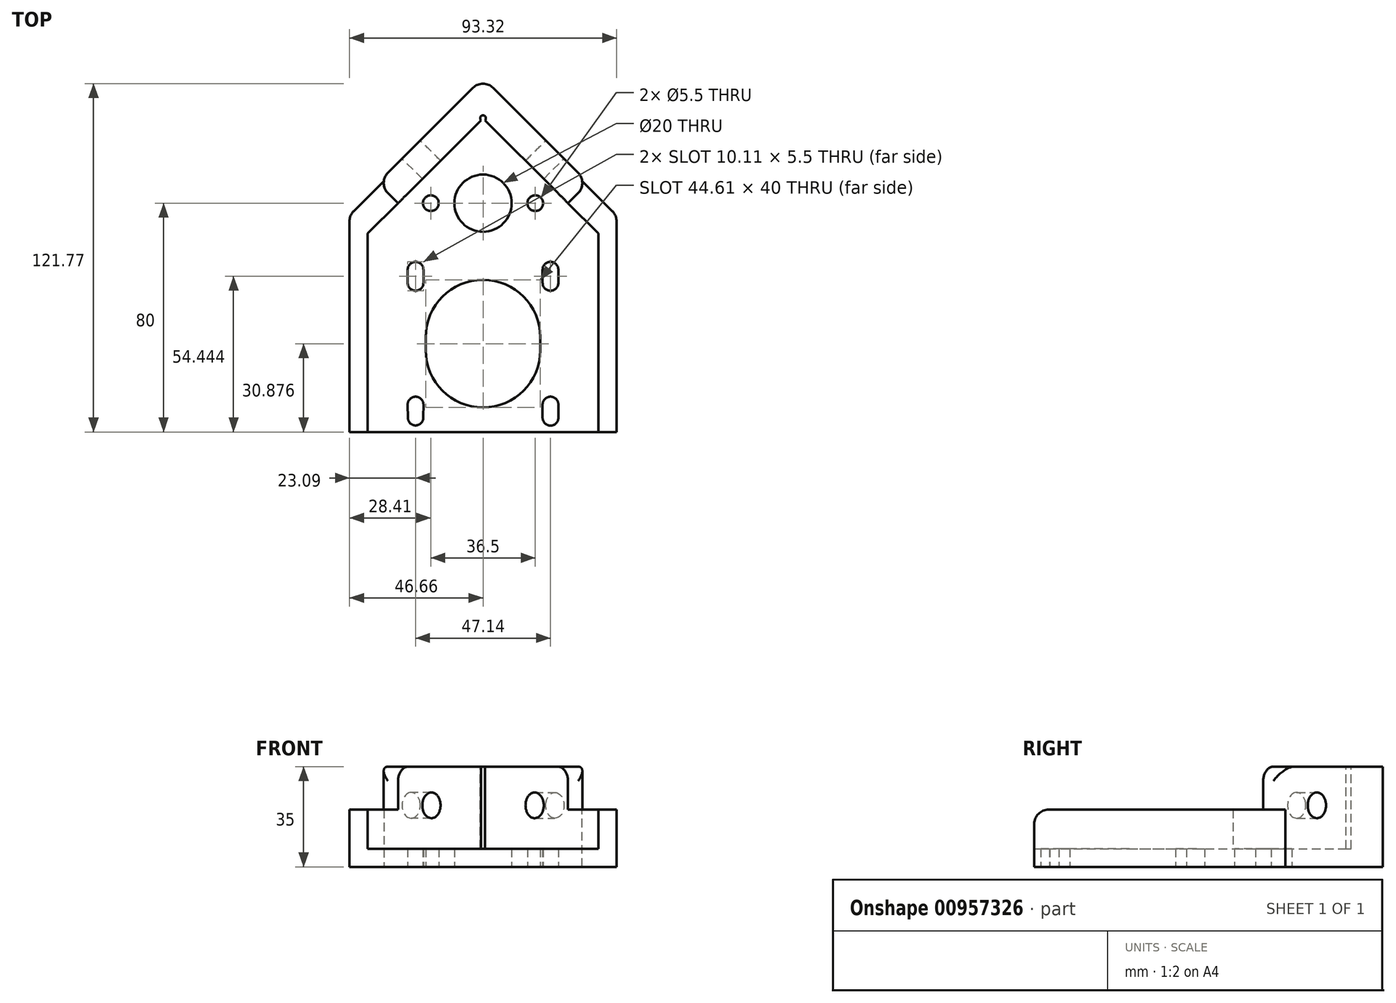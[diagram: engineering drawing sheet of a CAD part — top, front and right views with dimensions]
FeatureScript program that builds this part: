
annotation { "Feature Type Name" : "Feature", "Feature Type Description" : "" }
export const myFeature = defineFeature(function(context is Context, id is Id, definition is map)
    precondition{}
    {
        {
            var Q0;
            Q0=qCreatedBy(makeId("Top.planeOp"),FACE);
            var sketch = newSketch(context, id + "F0", { "sketchPlane" : qUnion([Q0])});
            skLineSegment(sketch, "E0", {"start": v(-29.7, 70) * mm, "end": v(0, 99.7) * mm});
            skLineSegment(sketch, "E1", {"start": v(0, 99.7) * mm, "end": v(0, 0) * mm, "construction": true});
            skCircle(sketch, "E2", {"center": v(0, 70) * mm, "radius": 10 * mm});
            skLineSegment(sketch, "E3", {"start": v(0, 70) * mm, "end": v(0, 99.7) * mm, "construction": true});
            skLineSegment(sketch, "E4", {"start": v(0, 99.7) * mm, "end": v(-29.7, 70) * mm, "construction": true});
            skLineSegment(sketch, "E5", {"start": v(-29.7, 70) * mm, "end": v(0, 40.3) * mm, "construction": true});
            skLineSegment(sketch, "E6", {"start": v(0, 88.25) * mm, "end": v(-18.25, 70) * mm, "construction": true});
            skLineSegment(sketch, "E7", {"start": v(-18.25, 70) * mm, "end": v(0, 51.75) * mm, "construction": true});
            skArc(sketch, "E8", {"start": v(-20.82, 46.75) * mm, "mid": v(-23.57, 49.5) * mm, "end": v(-26.32, 46.75) * mm});
            skCircle(sketch, "E9", {"center": v(-18.25, 70) * mm, "radius": 2.75 * mm});
            skLineSegment(sketch, "E10.MirrorCS", {"start": v(29.7, 70) * mm, "end": v(0, 99.7) * mm});
            skCircle(sketch, "E11.MirrorC", {"center": v(18.25, 70) * mm, "radius": 2.75 * mm});
            skArc(sketch, "E12.MirrorC", {"start": v(20.82, 46.75) * mm, "mid": v(23.57, 49.5) * mm, "end": v(26.32, 46.75) * mm});
            skLineSegment(sketch, "E13.MirrorCS", {"start": v(0, 99.7) * mm, "end": v(29.7, 70) * mm, "construction": true});
            skLineSegment(sketch, "E14.MirrorCS", {"start": v(0, 88.25) * mm, "end": v(18.25, 70) * mm, "construction": true});
            skLineSegment(sketch, "E15.MirrorCS", {"start": v(18.25, 70) * mm, "end": v(0, 51.75) * mm, "construction": true});
            skLineSegment(sketch, "E16.MirrorCS", {"start": v(29.7, 70) * mm, "end": v(0, 40.3) * mm, "construction": true});
            skLineSegment(sketch, "E17", {"start": v(-29.64, 23.18) * mm, "end": v(29.64, 23.18) * mm, "construction": true});
            skArc(sketch, "E18.MirrorC", {"start": v(26.32, -0.4) * mm, "mid": v(23.58, 2.36) * mm, "end": v(20.82, -0.39) * mm});
            skArc(sketch, "E19.MirrorC", {"start": v(-26.32, -0.42) * mm, "mid": v(-23.56, 2.36) * mm, "end": v(-20.82, -0.44) * mm});
            skLineSegment(sketch, "E20", {"start": v(-29.7, 70) * mm, "end": v(-29.7, -10) * mm});
            skLineSegment(sketch, "E21", {"start": v(-29.7, -10) * mm, "end": v(29.7, -10) * mm});
            skLineSegment(sketch, "E22", {"start": v(29.7, -10) * mm, "end": v(29.7, 70) * mm});
            skArc(sketch, "E23", {"start": v(-26.32, 42.14) * mm, "mid": v(-23.57, 39.39) * mm, "end": v(-20.82, 42.14) * mm});
            skArc(sketch, "E24.MirrorC", {"start": v(26.32, 42.14) * mm, "mid": v(23.57, 39.39) * mm, "end": v(20.82, 42.14) * mm});
            skArc(sketch, "E25.MirrorC", {"start": v(20.82, -5) * mm, "mid": v(23.78, -7.74) * mm, "end": v(26.3, -4.59) * mm});
            skArc(sketch, "E26.MirrorC", {"start": v(-20.9, -4.73) * mm, "mid": v(-23.42, -7.69) * mm, "end": v(-26.26, -5.03) * mm});
            skLineSegment(sketch, "E27", {"start": v(-26.32, 46.75) * mm, "end": v(-26.32, 42.14) * mm});
            skLineSegment(sketch, "E28", {"start": v(-20.82, 46.75) * mm, "end": v(-20.82, 42.14) * mm});
            skLineSegment(sketch, "E29", {"start": v(20.82, 46.75) * mm, "end": v(20.82, 42.14) * mm});
            skLineSegment(sketch, "E30", {"start": v(26.32, 46.75) * mm, "end": v(26.32, 42.14) * mm});
            skLineSegment(sketch, "E31", {"start": v(-26.32, -0.42) * mm, "end": v(-26.26, -5.03) * mm});
            skLineSegment(sketch, "E32", {"start": v(-20.82, -0.44) * mm, "end": v(-20.9, -4.73) * mm});
            skLineSegment(sketch, "E33", {"start": v(20.82, -0.39) * mm, "end": v(20.82, -5) * mm});
            skLineSegment(sketch, "E34", {"start": v(26.32, -0.4) * mm, "end": v(26.3, -4.59) * mm});
            skArc(sketch, "E35", {"start": v(20, 23.18) * mm, "mid": v(0, 43.18) * mm, "end": v(-20, 23.18) * mm});
            skArc(sketch, "E36", {"start": v(-20, 18.57) * mm, "mid": v(0, -1.43) * mm, "end": v(20, 18.57) * mm});
            skLineSegment(sketch, "E37", {"start": v(-20, 23.18) * mm, "end": v(-20, 18.57) * mm});
            skLineSegment(sketch, "E38", {"start": v(20, 23.18) * mm, "end": v(20, 18.57) * mm});
            skSolve(sketch);
        }
        {
            var Q0;
            Q0=makeQuery(id+"F0.imprint","IMPRINT",FACE,{"disambiguationData":[TD([[makeQuery(id+"F0.imprint","IMPRINT",EDGE,{"derivedFrom":sQuery(id+"F0.wireOp",EDGE,"E0")}),-1.0]])]});
            extrude(context, id + "F1", {"entities" : qUnion([Q0]), "depth" : 6.35 * mm, "offsetDistance" : 25 * mm});
        }
        {
            var Q0;
            Q0=qCreatedBy(makeId("Top.planeOp"),FACE);
            var sketch = newSketch(context, id + "F2", { "sketchPlane" : qUnion([Q0])});
            skLineSegment(sketch, "E39", {"start": v(0, 99.7) * mm, "end": v(-46.66, 53.04) * mm});
            skLineSegment(sketch, "E40", {"start": v(-46.66, 53.04) * mm, "end": v(-46.66, -10) * mm});
            skLineSegment(sketch, "E41", {"start": v(-46.66, -10) * mm, "end": v(0, -10) * mm});
            skLineSegment(sketch, "E42", {"start": v(-40.3, 59.4) * mm, "end": v(-40.3, -10) * mm});
            skLineSegment(sketch, "E43", {"start": v(0, 99.7) * mm, "end": v(0, 112.43) * mm});
            skLineSegment(sketch, "E44", {"start": v(0, 112.43) * mm, "end": v(-46.66, 65.77) * mm});
            skLineSegment(sketch, "E45", {"start": v(-46.66, 65.77) * mm, "end": v(-46.66, 53.04) * mm});
            skLineSegment(sketch, "E46.MirrorCS", {"start": v(0, 99.7) * mm, "end": v(46.66, 53.04) * mm});
            skLineSegment(sketch, "E47.MirrorCS", {"start": v(40.3, 59.4) * mm, "end": v(40.3, -10) * mm});
            skLineSegment(sketch, "E48.MirrorCS", {"start": v(0, 112.43) * mm, "end": v(46.66, 65.77) * mm});
            skLineSegment(sketch, "E49.MirrorCS", {"start": v(46.66, 53.04) * mm, "end": v(46.66, -10) * mm});
            skLineSegment(sketch, "E50.MirrorCS", {"start": v(46.66, -10) * mm, "end": v(0, -10) * mm});
            skLineSegment(sketch, "E51.MirrorCS", {"start": v(46.66, 65.77) * mm, "end": v(46.66, 53.04) * mm});
            skLineSegment(sketch, "E52", {"start": v(-29.7, 70) * mm, "end": v(-29.7, -10) * mm});
            skLineSegment(sketch, "E53", {"start": v(29.7, 70) * mm, "end": v(29.7, -10) * mm});
            skSolve(sketch);
        }
        {
            var Q0;
            Q0=makeQuery(id+"F2.imprint","IMPRINT",FACE,{"disambiguationData":[TD([[makeQuery(id+"F2.imprint","IMPRINT",EDGE,{"derivedFrom":sQuery(id+"F2.wireOp",EDGE,"E44")}),1.0]])]});
            var Q1;
            {var subQ0=sQuery(id+"F2.wireOp",EDGE,"E42");Q1=makeQuery(id+"F2.imprint","IMPRINT",FACE,{"disambiguationData":[TD([[makeQuery(id+"F2.imprint","IMPRINT",EDGE,{"derivedFrom":subQ0}),1.0]])]});}
            var Q2;
            {var subQ0=sQuery(id+"F2.wireOp",EDGE,"E40");Q2=makeQuery(id+"F2.imprint","IMPRINT",FACE,{"disambiguationData":[TD([[makeQuery(id+"F2.imprint","IMPRINT",EDGE,{"derivedFrom":subQ0}),1.0]])]});}
            var Q3;
            {var subQ0=sQuery(id+"F2.wireOp",EDGE,"E47.MirrorCS");Q3=makeQuery(id+"F2.imprint","IMPRINT",FACE,{"disambiguationData":[TD([[makeQuery(id+"F2.imprint","IMPRINT",EDGE,{"derivedFrom":subQ0}),-1.0]])]});}
            var Q4;
            {var subQ2=sQuery(id+"F2.wireOp",EDGE,"E47.MirrorCS");Q4=makeQuery(id+"F2.imprint","IMPRINT",FACE,{"disambiguationData":[TD([[makeQuery(id+"F2.imprint","IMPRINT",EDGE,{"derivedFrom":subQ2}),1.0]])]});}
            var Q5;
            Q5=makeQuery(id+"F2.imprint","IMPRINT",FACE,{"disambiguationData":[TD([[makeQuery(id+"F2.imprint","IMPRINT",EDGE,{"derivedFrom":sQuery(id+"F2.wireOp",EDGE,"E48.MirrorCS")}),-1.0]])]});
            extrude(context, id + "F3", {"entities" : qUnion([Q0, Q1, Q2, Q3, Q4, Q5]), "operationType" : NewBodyOperationType.ADD, "depth" : 6.35 * mm, "offsetDistance" : 25 * mm});
        }
        {
            var Q0;
            {var subQ2=sQuery(id+"F2.wireOp",EDGE,"E47.MirrorCS");Q0=makeQuery(id+"F2.imprint","IMPRINT",FACE,{"disambiguationData":[TD([[makeQuery(id+"F2.imprint","IMPRINT",EDGE,{"derivedFrom":subQ2}),1.0]])]});}
            var Q1;
            {var subQ0=sQuery(id+"F2.wireOp",EDGE,"E40");Q1=makeQuery(id+"F2.imprint","IMPRINT",FACE,{"disambiguationData":[TD([[makeQuery(id+"F2.imprint","IMPRINT",EDGE,{"derivedFrom":subQ0}),1.0]])]});}
            var Q2;
            Q2=makeQuery(id+"F2.imprint","IMPRINT",FACE,{"disambiguationData":[TD([[makeQuery(id+"F2.imprint","IMPRINT",EDGE,{"derivedFrom":sQuery(id+"F2.wireOp",EDGE,"E48.MirrorCS")}),-1.0]])]});
            var Q3;
            Q3=makeQuery(id+"F2.imprint","IMPRINT",FACE,{"disambiguationData":[TD([[makeQuery(id+"F2.imprint","IMPRINT",EDGE,{"derivedFrom":sQuery(id+"F2.wireOp",EDGE,"E44")}),1.0]])]});
            extrude(context, id + "F4", {"entities" : qUnion([Q0, Q1, Q2, Q3]), "operationType" : NewBodyOperationType.ADD, "depth" : 20 * mm, "offsetDistance" : 25 * mm});
        }
        {
            var Q0;
            Q0=makeQuery(id+"F1.opExtrude","CAP_FACE",FACE,{"disambiguationData":[OSD([sQuery(id+"F0.wireOp",EDGE,"CqNvWhCR-X9q0-hkb6-Y5B6-FddO2p67PmDH"),sQuery(id+"F0.wireOp",EDGE,"OIBRXke7-KifX-nYgX-6AyS-i8wfslzJrOtY"),sQuery(id+"F0.wireOp",EDGE,"E0"),sQuery(id+"F0.wireOp",EDGE,"E2"),sQuery(id+"F0.wireOp",EDGE,"E8"),sQuery(id+"F0.wireOp",EDGE,"E9"),sQuery(id+"F0.wireOp",EDGE,"E10.MirrorCS"),sQuery(id+"F0.wireOp",EDGE,"2e774edb-d105-46dc-81d8-f344b8156d9b1.MirrorCS"),sQuery(id+"F0.wireOp",EDGE,"2e774edb-d105-46dc-81d8-f344b8156d9b2.MirrorCS"),sQuery(id+"F0.wireOp",EDGE,"2e774edb-d105-46dc-81d8-f344b8156d9b3.MirrorC"),sQuery(id+"F0.wireOp",EDGE,"2e774edb-d105-46dc-81d8-f344b8156d9b6.MirrorC"),sQuery(id+"F0.wireOp",EDGE,"E11.MirrorC"),sQuery(id+"F0.wireOp",EDGE,"E12.MirrorC")])],"isStart":true});
            var sketch = newSketch(context, id + "F5", { "sketchPlane" : qUnion([Q0])});
            skLineSegment(sketch, "E54", {"start": v(-29.7, -70) * mm, "end": v(-36.77, -77.07) * mm});
            skLineSegment(sketch, "E55", {"start": v(-36.77, -77.07) * mm, "end": v(-5.84, -108) * mm});
            skLineSegment(sketch, "E56", {"start": v(0, -70) * mm, "end": v(-10, -70) * mm, "construction": true});
            skLineSegment(sketch, "E57", {"start": v(0, -108) * mm, "end": v(0, -70) * mm, "construction": true});
            skLineSegment(sketch, "E58.MirrorCS", {"start": v(0, -70) * mm, "end": v(10, -70) * mm, "construction": true});
            skLineSegment(sketch, "E59.MirrorCS", {"start": v(36.77, -77.07) * mm, "end": v(5.84, -108) * mm});
            skLineSegment(sketch, "E60.MirrorCS", {"start": v(29.7, -70) * mm, "end": v(36.77, -77.07) * mm});
            skLineSegment(sketch, "E61", {"start": v(-29.7, -70) * mm, "end": v(0, -99.7) * mm});
            skLineSegment(sketch, "E62", {"start": v(0, -99.7) * mm, "end": v(29.7, -70) * mm});
            skLineSegment(sketch, "E63", {"start": v(-5.84, -108) * mm, "end": v(0, -113.84) * mm});
            skLineSegment(sketch, "E64", {"start": v(0, -113.84) * mm, "end": v(5.84, -108) * mm});
            skSolve(sketch);
        }
        {
            var Q0;
            Q0=qSketchRegion(id+"F5",true);
            extrude(context, id + "F6", {"entities" : qUnion([Q0]), "operationType" : NewBodyOperationType.ADD, "oppositeDirection" : true, "depth" : 35 * mm, "offsetDistance" : 25 * mm});
        }
        {
            var Q0;
            Q0=makeQuery(id+"F6.opExtrude","SWEPT_FACE",FACE,{"disambiguationData":[OSD([sQuery(id+"F5.wireOp",EDGE,"E59.MirrorCS")])]});
            var sketch = newSketch(context, id + "F7", { "sketchPlane" : qUnion([Q0])});
            skCircle(sketch, "E65", {"center": v(45, 21.5) * mm, "radius": 4.5 * mm});
            skSolve(sketch);
        }
        {
            var Q0;
            Q0=qSketchRegion(id+"F7",true);
            extrude(context, id + "F8", {"entities" : qUnion([Q0]), "oppositeDirection" : true, "depth" : 12.6 * mm, "offsetDistance" : 25 * mm});
        }
        {
            var Q0;
            Q0=makeQuery(id+"F6.opExtrude","CAP_EDGE",EDGE,{"disambiguationData":[OSD([sQuery(id+"F5.wireOp",EDGE,"E60.MirrorCS")])],"isStart":false});
            var Q1;
            Q1=makeQuery(id+"F6.opExtrude","CAP_EDGE",EDGE,{"disambiguationData":[OSD([sQuery(id+"F5.wireOp",EDGE,"E54")])],"isStart":false});
            var Q2;
            Q2=makeQuery(id+"F6.opExtrude","SWEPT_EDGE",EDGE,{"disambiguationData":[OSD([sQuery(id+"F5.wireOp",EDGE,"E55"),sQuery(id+"F5.wireOp",EDGE,"w3E64LNr-WMrx-ZLcy-Yoss-pTT7xmLwoX0f")])]});
            var Q3;
            Q3=makeQuery(id+"F6.opExtrude","SWEPT_EDGE",EDGE,{"disambiguationData":[OSD([sQuery(id+"F5.wireOp",EDGE,"90518d0a-a1d5-48df-ab97-8c912662351c1.MirrorCS"),sQuery(id+"F5.wireOp",EDGE,"E59.MirrorCS")])]});
            var Q4;
            Q4=makeQuery(id+"F4.opExtrude","SWEPT_EDGE",EDGE,{"disambiguationData":[OSD([sQuery(id+"F2.wireOp",EDGE,"2lfpNZEj-ZkGW-H239-BTSb-PnOlReioI05R"),sQuery(id+"F2.wireOp",EDGE,"Y7oqJvWZ-fw66-fsUm-KreW-a8dZiDZSDvyh")])]});
            var Q5;
            Q5=makeQuery(id+"F4.opExtrude","SWEPT_EDGE",EDGE,{"disambiguationData":[OSD([sQuery(id+"F2.wireOp",EDGE,"28NQsGmG-He18-9Lgd-yZ6g-9qgcsKt1NNAv"),sQuery(id+"F2.wireOp",EDGE,"8z5xyMcj-PstS-gyoc-Zbjk-fvMzcH1uuJEM"),sQuery(id+"F2.wireOp",EDGE,"Y7oqJvWZ-fw66-fsUm-KreW-a8dZiDZSDvyh")])]});
            var Q6;
            Q6=makeQuery(id+"F4.opExtrude","SWEPT_EDGE",EDGE,{"disambiguationData":[OSD([sQuery(id+"F2.wireOp",EDGE,"f8a4cf56-4e17-4c88-a3d7-404ae4d5c7f90.MirrorCS"),sQuery(id+"F2.wireOp",EDGE,"8ee5f7fc-c1b9-4571-8d56-7bdf9bbc2ac70.MirrorCS")])]});
            var Q7;
            Q7=makeQuery(id+"F4.opExtrude","SWEPT_EDGE",EDGE,{"disambiguationData":[OSD([sQuery(id+"F2.wireOp",EDGE,"1d0ece78-aebc-48e7-a5a8-8e38171d103b0.MirrorCS"),sQuery(id+"F2.wireOp",EDGE,"a64d8b8a-c93f-4d5a-9a8b-79496ac34db30.MirrorCS"),sQuery(id+"F2.wireOp",EDGE,"8ee5f7fc-c1b9-4571-8d56-7bdf9bbc2ac70.MirrorCS")])]});
            var Q8;
            Q8=makeQuery(id+"F4.opExtrude","CAP_EDGE",EDGE,{"disambiguationData":[OSD([sQuery(id+"F2.wireOp",EDGE,"E50.MirrorCS")])],"isStart":false});
            var Q9;
            Q9=makeQuery(id+"F4.opExtrude","CAP_EDGE",EDGE,{"disambiguationData":[OSD([sQuery(id+"F2.wireOp",EDGE,"E41")])],"isStart":false});
            var Q10;
            {var subQ0=sQuery(id+"F2.wireOp",EDGE,"E51.MirrorCS");var subQ1=sQuery(id+"F2.wireOp",EDGE,"E48.MirrorCS");Q10=makeQuery(id+"F4.boolean.opBoolean","MERGE",EDGE,{"derivedFrom":[makeQuery(id+"F3.opExtrude","SWEPT_EDGE",EDGE,{"disambiguationData":[OSD([subQ1,subQ0])]}),makeQuery(id+"F4.opExtrude","SWEPT_EDGE",EDGE,{"disambiguationData":[OSD([subQ1,subQ0])]})]});}
            var Q11;
            Q11=makeQuery(id+"F6.opExtrude","SWEPT_EDGE",EDGE,{"disambiguationData":[OSD([sQuery(id+"F5.wireOp",EDGE,"E63"),sQuery(id+"F5.wireOp",EDGE,"E64")])]});
            var Q12;
            {var subQ0=sQuery(id+"F2.wireOp",EDGE,"E45");var subQ1=sQuery(id+"F2.wireOp",EDGE,"E44");Q12=makeQuery(id+"F4.boolean.opBoolean","MERGE",EDGE,{"derivedFrom":[makeQuery(id+"F3.opExtrude","SWEPT_EDGE",EDGE,{"disambiguationData":[OSD([subQ1,subQ0])]}),makeQuery(id+"F4.opExtrude","SWEPT_EDGE",EDGE,{"disambiguationData":[OSD([subQ1,subQ0])]})]});}
            fillet(context, id + "F9", {"entities" : qUnion([Q0, Q1, Q2, Q3, Q4, Q5, Q6, Q7, Q8, Q9, Q10, Q11, Q12]), "radius" : 5 * mm, "tangentPropagation" : true, "defaultsChanged" : false, "vertexSettings" : [], "allowEdgeOverflow" : false});
        }
        {
            var Q0;
            Q0=makeQuery(id+"F6.opExtrude","CAP_FACE",FACE,{"disambiguationData":[OSD([sQuery(id+"F5.wireOp",EDGE,"E54"),sQuery(id+"F5.wireOp",EDGE,"E55"),sQuery(id+"F5.wireOp",EDGE,"w3E64LNr-WMrx-ZLcy-Yoss-pTT7xmLwoX0f"),sQuery(id+"F5.wireOp",EDGE,"90518d0a-a1d5-48df-ab97-8c912662351c1.MirrorCS"),sQuery(id+"F5.wireOp",EDGE,"E59.MirrorCS"),sQuery(id+"F5.wireOp",EDGE,"E60.MirrorCS"),sQuery(id+"F5.wireOp",EDGE,"E61"),sQuery(id+"F5.wireOp",EDGE,"E62")])],"isStart":false});
            var sketch = newSketch(context, id + "F10", { "sketchPlane" : qUnion([Q0])});
            skCircle(sketch, "E66", {"center": v(0, 99.7) * mm, "radius": 1 * mm});
            skSolve(sketch);
        }
        {
            var Q0;
            Q0=qSketchRegion(id+"F10",true);
            var Q1;
            Q1=makeQuery(id+"F1.opExtrude","CAP_FACE",FACE,{"disambiguationData":[OSD([sQuery(id+"F0.wireOp",EDGE,"CqNvWhCR-X9q0-hkb6-Y5B6-FddO2p67PmDH"),sQuery(id+"F0.wireOp",EDGE,"OIBRXke7-KifX-nYgX-6AyS-i8wfslzJrOtY"),sQuery(id+"F0.wireOp",EDGE,"E0"),sQuery(id+"F0.wireOp",EDGE,"E2"),sQuery(id+"F0.wireOp",EDGE,"E8"),sQuery(id+"F0.wireOp",EDGE,"E9"),sQuery(id+"F0.wireOp",EDGE,"E10.MirrorCS"),sQuery(id+"F0.wireOp",EDGE,"2e774edb-d105-46dc-81d8-f344b8156d9b1.MirrorCS"),sQuery(id+"F0.wireOp",EDGE,"2e774edb-d105-46dc-81d8-f344b8156d9b2.MirrorCS"),sQuery(id+"F0.wireOp",EDGE,"2e774edb-d105-46dc-81d8-f344b8156d9b3.MirrorC"),sQuery(id+"F0.wireOp",EDGE,"2e774edb-d105-46dc-81d8-f344b8156d9b6.MirrorC"),sQuery(id+"F0.wireOp",EDGE,"E11.MirrorC"),sQuery(id+"F0.wireOp",EDGE,"E12.MirrorC")])],"isStart":false});
            extrude(context, id + "F11", {"entities" : qUnion([Q0]), "operationType" : NewBodyOperationType.REMOVE, "endBound" : BoundingType.UP_TO_SURFACE, "oppositeDirection" : true, "depth" : 25 * mm, "endBoundEntityFace" : qUnion([Q1]), "offsetDistance" : 25 * mm});
        }
        {
            var Q0;
            Q0=makeQuery(id+"F8.opExtrude","SWEPT_BODY",BODY,{"disambiguationData":[OSD([sQuery(id+"F7.wireOp",EDGE,"E65")])]});
            var Q1;
            Q1=qCreatedBy(makeId("Right.planeOp"),FACE);
            mirror(context, id + "F12", {"entities" : qUnion([Q0]), "mirrorPlane" : qUnion([Q1])});
        }
        {
            var Q0;
            Q0=makeQuery(id+"F12.opPattern","COPY",BODY,{"derivedFrom":makeQuery(id+"F8.opExtrude","SWEPT_BODY",BODY,{"disambiguationData":[OSD([sQuery(id+"F7.wireOp",EDGE,"E65")])]}),"instanceName":"1"});
            var Q1;
            Q1=makeQuery(id+"F8.opExtrude","SWEPT_BODY",BODY,{"disambiguationData":[OSD([sQuery(id+"F7.wireOp",EDGE,"E65")])]});
            var Q2;
            Q2=makeQuery(id+"F1.opExtrude","SWEPT_BODY",BODY,{"disambiguationData":[OSD([sQuery(id+"F0.wireOp",EDGE,"E0"),sQuery(id+"F0.wireOp",EDGE,"E2"),sQuery(id+"F0.wireOp",EDGE,"E8"),sQuery(id+"F0.wireOp",EDGE,"E9"),sQuery(id+"F0.wireOp",EDGE,"E10.MirrorCS"),sQuery(id+"F0.wireOp",EDGE,"E11.MirrorC"),sQuery(id+"F0.wireOp",EDGE,"E12.MirrorC"),sQuery(id+"F0.wireOp",EDGE,"E18.MirrorC"),sQuery(id+"F0.wireOp",EDGE,"E19.MirrorC"),sQuery(id+"F0.wireOp",EDGE,"E20"),sQuery(id+"F0.wireOp",EDGE,"E21"),sQuery(id+"F0.wireOp",EDGE,"E22"),sQuery(id+"F0.wireOp",EDGE,"E23"),sQuery(id+"F0.wireOp",EDGE,"E24.MirrorC"),sQuery(id+"F0.wireOp",EDGE,"E25.MirrorC"),sQuery(id+"F0.wireOp",EDGE,"E26.MirrorC"),sQuery(id+"F0.wireOp",EDGE,"E27"),sQuery(id+"F0.wireOp",EDGE,"E28"),sQuery(id+"F0.wireOp",EDGE,"E29"),sQuery(id+"F0.wireOp",EDGE,"E30"),sQuery(id+"F0.wireOp",EDGE,"E31"),sQuery(id+"F0.wireOp",EDGE,"E32"),sQuery(id+"F0.wireOp",EDGE,"E33"),sQuery(id+"F0.wireOp",EDGE,"E34"),sQuery(id+"F0.wireOp",EDGE,"E35"),sQuery(id+"F0.wireOp",EDGE,"E36"),sQuery(id+"F0.wireOp",EDGE,"E37"),sQuery(id+"F0.wireOp",EDGE,"E38")])]});
            booleanBodies(context, id + "F13", {"operationType" : BooleanOperationType.SUBTRACTION, "tools" : qUnion([Q0, Q1]), "targets" : qUnion([Q2])});
        }
    });
